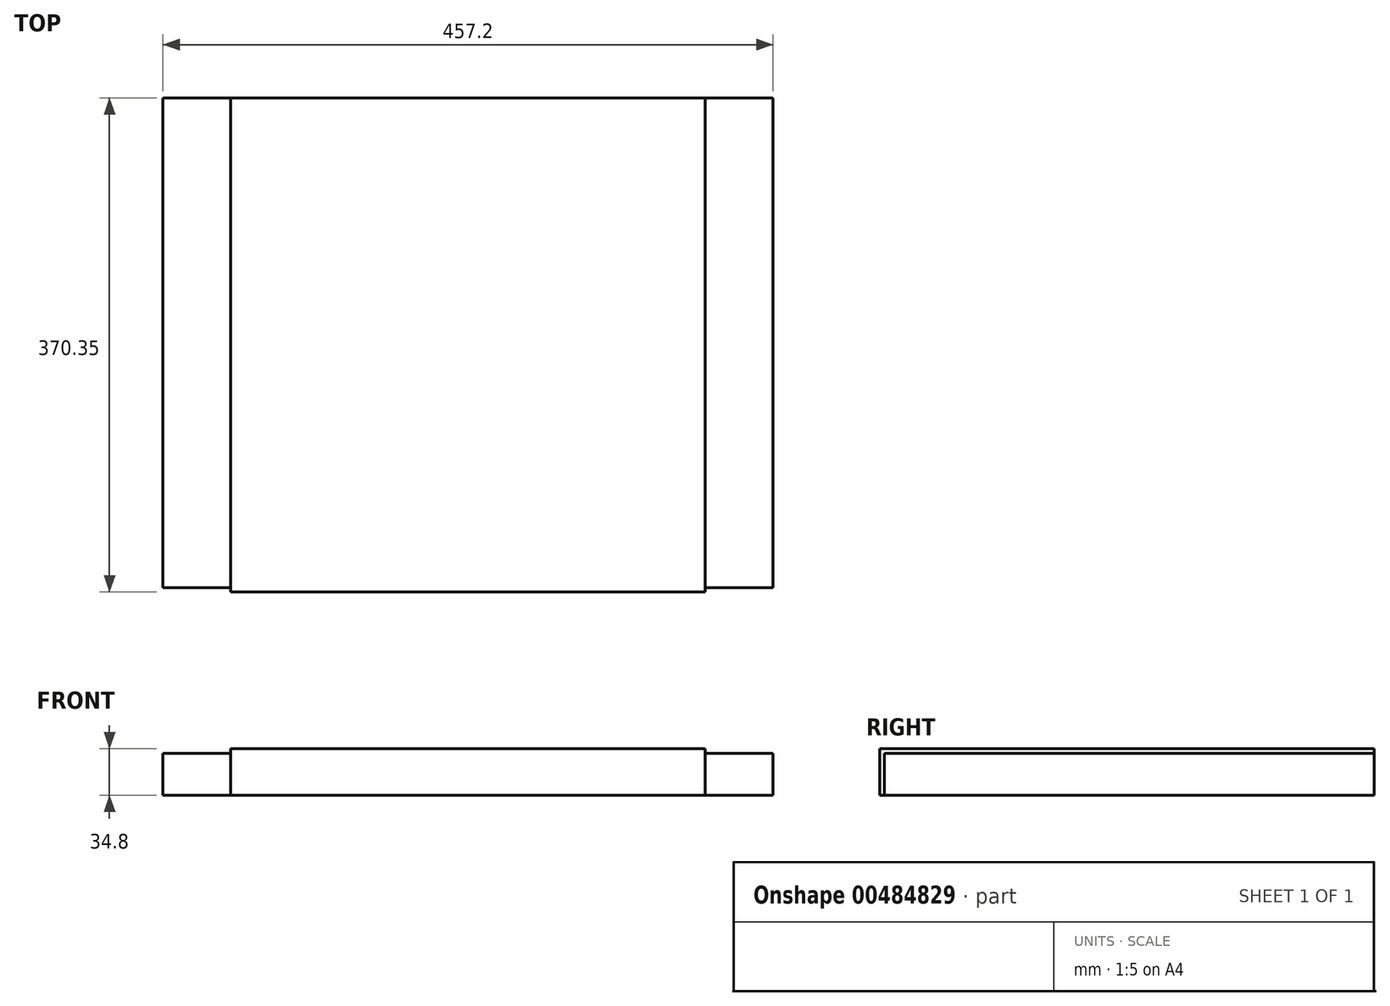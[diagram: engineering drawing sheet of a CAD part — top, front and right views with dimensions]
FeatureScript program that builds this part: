
annotation { "Feature Type Name" : "Feature", "Feature Type Description" : "" }
export const myFeature = defineFeature(function(context is Context, id is Id, definition is map)
    precondition{}
    {
        {
            var Q0;
            Q0=qCreatedBy(makeId("Right.planeOp"),FACE);
            var sketch = newSketch(context, id + "F0", { "sketchPlane" : qUnion([Q0])});
            skLineSegment(sketch, "E0.bottom", {"start": v(183.52, 15.75) * mm, "end": v(-183.52, 15.75) * mm});
            skLineSegment(sketch, "E0.top", {"start": v(183.52, -15.75) * mm, "end": v(-183.52, -15.75) * mm});
            skLineSegment(sketch, "E0.left", {"start": v(183.52, 15.75) * mm, "end": v(183.52, -15.75) * mm});
            skLineSegment(sketch, "E0.right", {"start": v(-183.52, 15.75) * mm, "end": v(-183.52, -15.75) * mm});
            skPoint(sketch, "E0.middle", {"position": v(0, 0) * mm});
            skSolve(sketch);
        }
        {
            var Q0;
            Q0 = qSketchRegion(id + "F0", true);
            extrude(context, id + "F1", {"entities" : qUnion([Q0]), "depth" : 457.2 * mm});
        }
        {
            var Q0;
            Q0=makeQuery(id+"F1.opExtrude","SWEPT_FACE",FACE,{"disambiguationData":[OSD([sQuery(id+"F0.wireOp",EDGE,"E0.bottom")])]});
            var sketch = newSketch(context, id + "F2", { "sketchPlane" : qUnion([Q0])});
            skLineSegment(sketch, "E1.bottom", {"start": v(406.4, 183.52) * mm, "end": v(50.8, 183.52) * mm});
            skLineSegment(sketch, "E1.top", {"start": v(406.4, -183.52) * mm, "end": v(50.8, -183.52) * mm});
            skLineSegment(sketch, "E1.left", {"start": v(406.4, 183.52) * mm, "end": v(406.4, -183.52) * mm});
            skLineSegment(sketch, "E1.right", {"start": v(50.8, 183.52) * mm, "end": v(50.8, -183.52) * mm});
            skPoint(sketch, "E1.middle", {"position": v(228.6, 0) * mm});
            skSolve(sketch);
        }
        {
            var Q0;
            Q0 = qSketchRegion(id + "F2", true);
            extrude(context, id + "F3", {"entities" : qUnion([Q0]), "operationType" : NewBodyOperationType.ADD, "depth" : 3.3 * mm});
        }
        {
            var Q0;
            Q0=makeQuery(id+"F3.boolean.opBoolean","MERGE",FACE,{"derivedFrom":[makeQuery(id+"F1.opExtrude","SWEPT_FACE",FACE,{"disambiguationData":[OSD([sQuery(id+"F0.wireOp",EDGE,"E0.right")])]}),makeQuery(id+"F3.opExtrude","SWEPT_FACE",FACE,{"disambiguationData":[OSD([sQuery(id+"F2.wireOp",EDGE,"E1.top")])]})]});
            var sketch = newSketch(context, id + "F4", { "sketchPlane" : qUnion([Q0])});
            skLineSegment(sketch, "E2.bottom", {"start": v(50.8, 19.05) * mm, "end": v(406.4, 19.05) * mm});
            skLineSegment(sketch, "E2.top", {"start": v(50.8, -15.75) * mm, "end": v(406.4, -15.75) * mm});
            skLineSegment(sketch, "E2.left", {"start": v(50.8, 19.05) * mm, "end": v(50.8, -15.75) * mm});
            skLineSegment(sketch, "E2.right", {"start": v(406.4, 19.05) * mm, "end": v(406.4, -15.75) * mm});
            skSolve(sketch);
        }
        {
            var Q0;
            Q0 = qSketchRegion(id + "F4", true);
            extrude(context, id + "F5", {"entities" : qUnion([Q0]), "operationType" : NewBodyOperationType.ADD, "depth" : 3.3 * mm});
        }
    });
